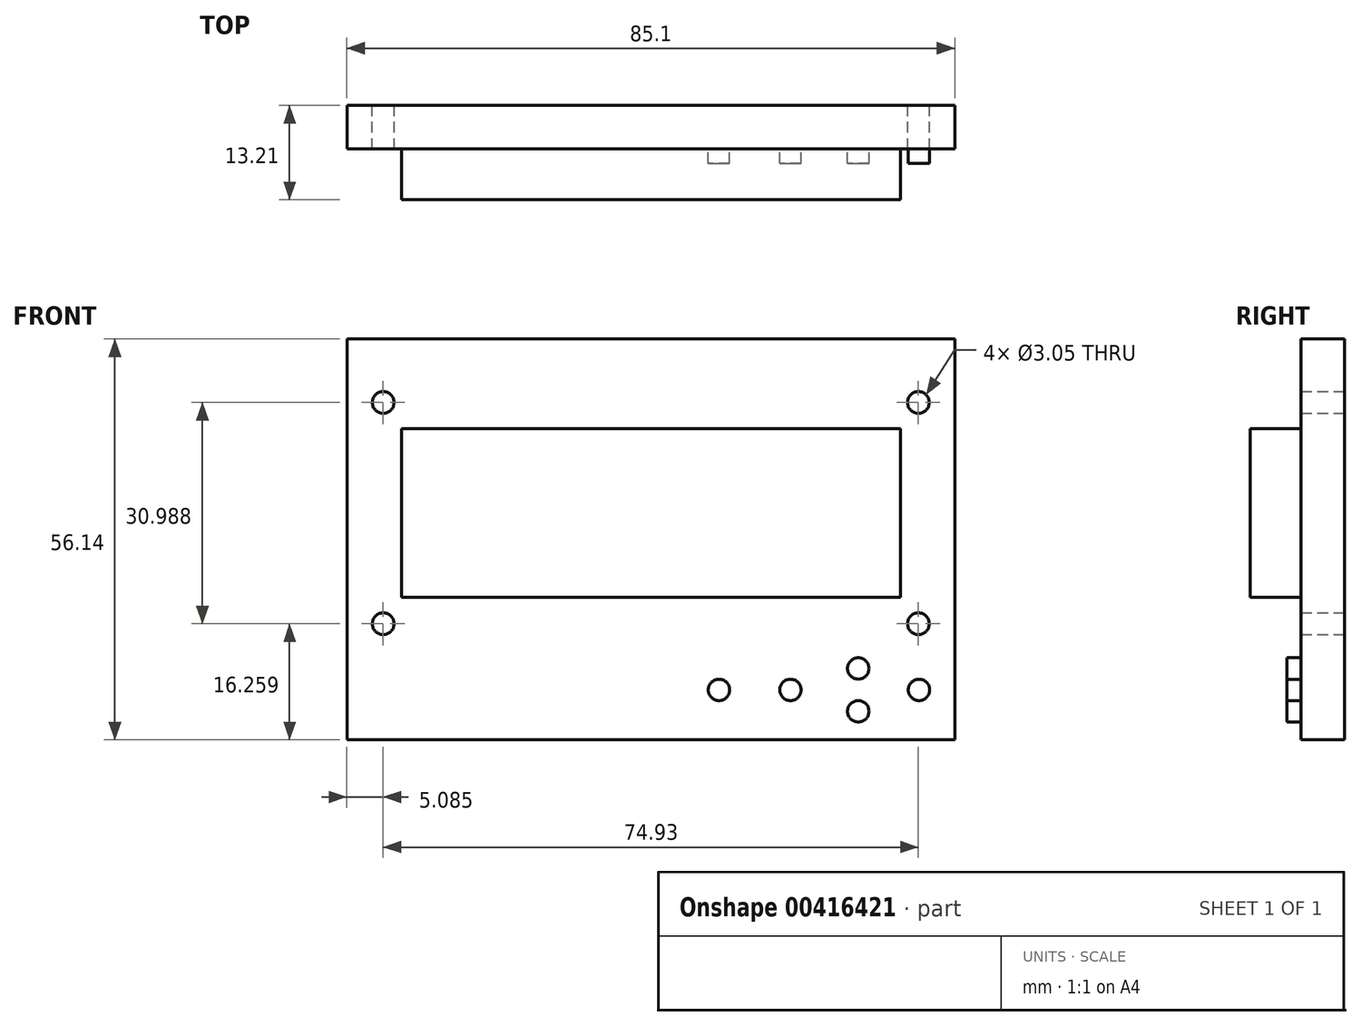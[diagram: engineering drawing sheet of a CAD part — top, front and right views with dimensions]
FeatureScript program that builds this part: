
annotation { "Feature Type Name" : "Feature", "Feature Type Description" : "" }
export const myFeature = defineFeature(function(context is Context, id is Id, definition is map)
    precondition{}
    {
        {
            var Q0;
            Q0=qCreatedBy(makeId("Front.planeOp"),FACE);
            var sketch = newSketch(context, id + "F0", { "sketchPlane" : qUnion([Q0])});
            skLineSegment(sketch, "E0.bottom", {"start": v(42.55, 28.07) * mm, "end": v(-42.55, 28.07) * mm});
            skLineSegment(sketch, "E0.top", {"start": v(42.55, -28.07) * mm, "end": v(-42.55, -28.07) * mm});
            skLineSegment(sketch, "E0.left", {"start": v(42.55, 28.07) * mm, "end": v(42.55, -28.07) * mm});
            skLineSegment(sketch, "E0.right", {"start": v(-42.55, 28.07) * mm, "end": v(-42.55, -28.07) * mm});
            skPoint(sketch, "E0.middle", {"position": v(0, 0) * mm});
            skCircle(sketch, "E1", {"center": v(-37.47, 19.18) * mm, "radius": 1.52 * mm});
            skCircle(sketch, "E2", {"center": v(37.46, 19.18) * mm, "radius": 1.52 * mm});
            skCircle(sketch, "E3", {"center": v(-37.47, -11.81) * mm, "radius": 1.52 * mm});
            skCircle(sketch, "E4", {"center": v(37.46, -11.81) * mm, "radius": 1.52 * mm});
            skSolve(sketch);
        }
        {
            var Q0;
            Q0=makeQuery(id+"F0.imprint","IMPRINT",FACE,{"disambiguationData":[TD([[makeQuery(id+"F0.imprint","IMPRINT",EDGE,{"derivedFrom":sQuery(id+"F0.wireOp",EDGE,"E0.bottom")}),1.0]])]});
            extrude(context, id + "F1", {"entities" : qUnion([Q0]), "depth" : 6.1 * mm});
        }
        {
            var Q0;
            Q0=makeQuery(id+"F1.opExtrude","CAP_FACE",FACE,{"disambiguationData":[OSD([sQuery(id+"F0.wireOp",EDGE,"E0.bottom"),sQuery(id+"F0.wireOp",EDGE,"E0.top"),sQuery(id+"F0.wireOp",EDGE,"E0.left"),sQuery(id+"F0.wireOp",EDGE,"E0.right"),sQuery(id+"F0.wireOp",EDGE,"E1"),sQuery(id+"F0.wireOp",EDGE,"E2"),sQuery(id+"F0.wireOp",EDGE,"E3"),sQuery(id+"F0.wireOp",EDGE,"E4")])],"isStart":false});
            var sketch = newSketch(context, id + "F2", { "sketchPlane" : qUnion([Q0])});
            skLineSegment(sketch, "E5.bottom", {"start": v(34.93, 15.5) * mm, "end": v(-34.93, 15.5) * mm});
            skLineSegment(sketch, "E5.top", {"start": v(34.93, -8.13) * mm, "end": v(-34.93, -8.13) * mm});
            skLineSegment(sketch, "E5.left", {"start": v(34.93, 15.5) * mm, "end": v(34.93, -8.13) * mm});
            skLineSegment(sketch, "E5.right", {"start": v(-34.93, 15.5) * mm, "end": v(-34.93, -8.13) * mm});
            skPoint(sketch, "E5.middle", {"position": v(0, 3.68) * mm});
            skSolve(sketch);
        }
        {
            var Q0;
            Q0=makeQuery(id+"F2.imprint","IMPRINT",FACE,{"disambiguationData":[TD([[makeQuery(id+"F2.imprint","IMPRINT",EDGE,{"derivedFrom":sQuery(id+"F2.wireOp",EDGE,"E5.bottom")}),1.0]])]});
            extrude(context, id + "F3", {"entities" : qUnion([Q0]), "operationType" : NewBodyOperationType.ADD, "depth" : 7.11 * mm});
        }
        {
            var Q0;
            Q0=makeQuery(id+"F1.opExtrude","CAP_FACE",FACE,{"disambiguationData":[OSD([sQuery(id+"F0.wireOp",EDGE,"E0.bottom"),sQuery(id+"F0.wireOp",EDGE,"E0.top"),sQuery(id+"F0.wireOp",EDGE,"E0.left"),sQuery(id+"F0.wireOp",EDGE,"E0.right"),sQuery(id+"F0.wireOp",EDGE,"E1"),sQuery(id+"F0.wireOp",EDGE,"E2"),sQuery(id+"F0.wireOp",EDGE,"E3"),sQuery(id+"F0.wireOp",EDGE,"E4")])],"isStart":false});
            var sketch = newSketch(context, id + "F4", { "sketchPlane" : qUnion([Q0])});
            skCircle(sketch, "E6", {"center": v(9.55, -21.07) * mm, "radius": 1.5 * mm});
            skCircle(sketch, "E7", {"center": v(19.55, -21.07) * mm, "radius": 1.5 * mm});
            skCircle(sketch, "E8", {"center": v(29.05, -24.07) * mm, "radius": 1.5 * mm});
            skCircle(sketch, "E9", {"center": v(29.05, -18.07) * mm, "radius": 1.5 * mm});
            skCircle(sketch, "E10", {"center": v(37.55, -21.07) * mm, "radius": 1.5 * mm});
            skSolve(sketch);
        }
        {
            var Q0;
            Q0 = qSketchRegion(id + "F4", true);
            extrude(context, id + "F5", {"entities" : qUnion([Q0]), "operationType" : NewBodyOperationType.ADD, "depth" : 2 * mm});
        }
    });
